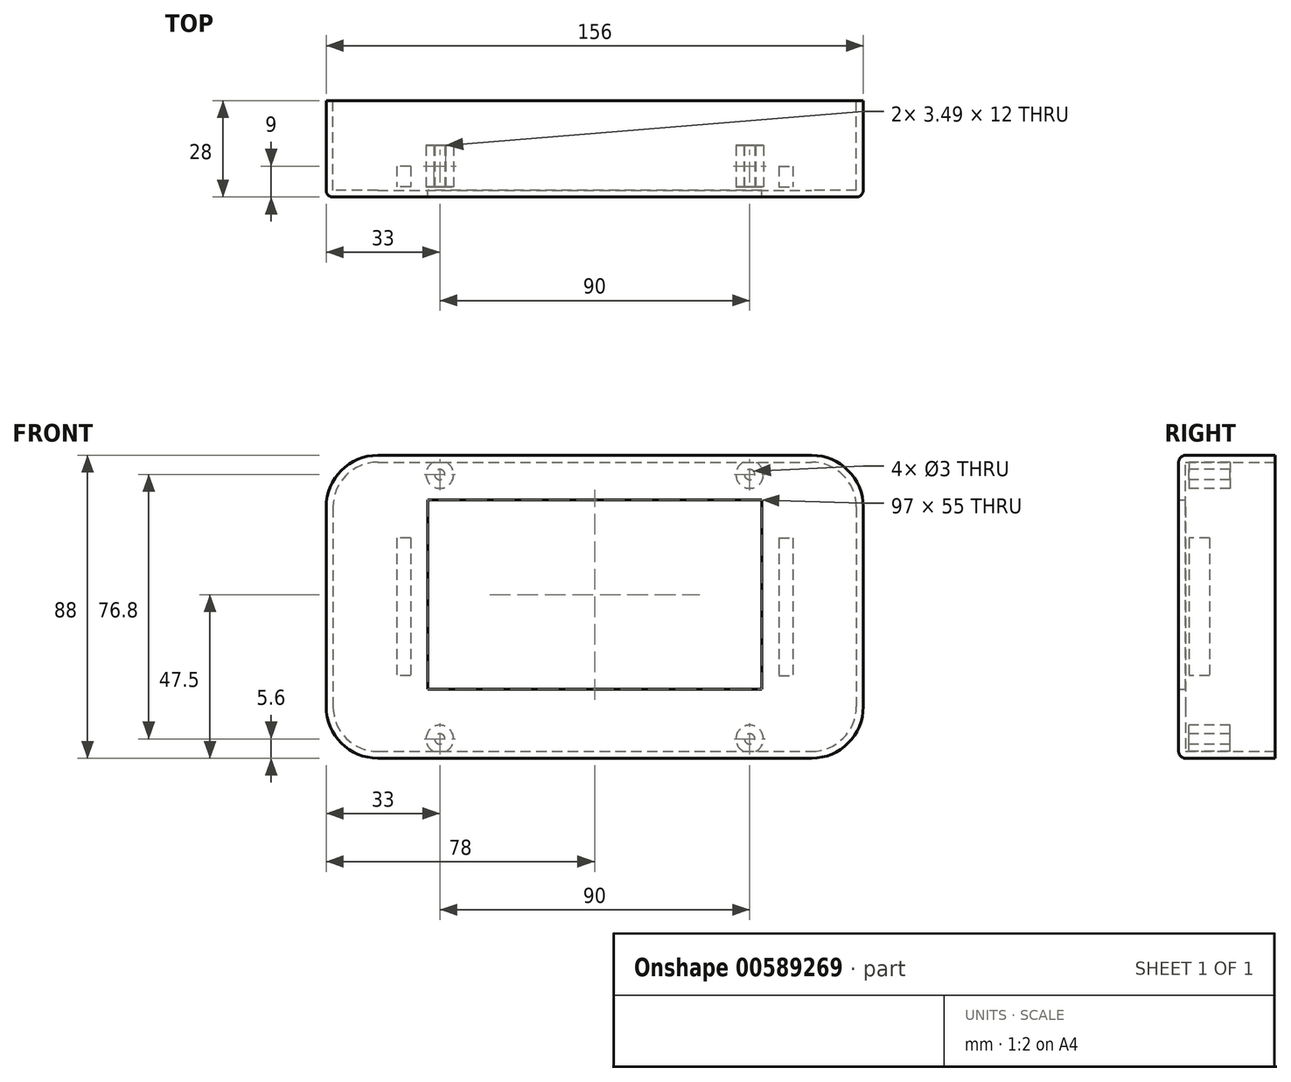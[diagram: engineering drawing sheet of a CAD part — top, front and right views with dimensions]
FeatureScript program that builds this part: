
annotation { "Feature Type Name" : "Feature", "Feature Type Description" : "" }
export const myFeature = defineFeature(function(context is Context, id is Id, definition is map)
    precondition{}
    {
        {
            var Q0;
            Q0=qCreatedBy(makeId("Front.planeOp"),FACE);
            var sketch = newSketch(context, id + "F0", { "sketchPlane" : qUnion([Q0])});
            skLineSegment(sketch, "E0.bottom", {"start": v(-63, 44) * mm, "end": v(63, 44) * mm});
            skLineSegment(sketch, "E0.top", {"start": v(-63, -44) * mm, "end": v(63, -44) * mm});
            skLineSegment(sketch, "E0.left", {"start": v(-78, 29) * mm, "end": v(-78, -29) * mm});
            skLineSegment(sketch, "E0.right", {"start": v(78, 29) * mm, "end": v(78, -29) * mm});
            skPoint(sketch, "E0.middle", {"position": v(0, 0) * mm});
            skPoint(sketch, "E1.visualSharp", {"position": v(-78, 44) * mm});
            skArc(sketch, "E1.filletArc", {"start": v(-63, 44) * mm, "mid": v(-73.6, 39.6) * mm, "end": v(-78, 29) * mm});
            skPoint(sketch, "E2.visualSharp", {"position": v(78, 44) * mm});
            skArc(sketch, "E2.filletArc", {"start": v(78, 29) * mm, "mid": v(73.6, 39.6) * mm, "end": v(63, 44) * mm});
            skPoint(sketch, "E3.visualSharp", {"position": v(78, -44) * mm});
            skArc(sketch, "E3.filletArc", {"start": v(63, -44) * mm, "mid": v(73.6, -39.6) * mm, "end": v(78, -29) * mm});
            skPoint(sketch, "E4.visualSharp", {"position": v(-78, -44) * mm});
            skArc(sketch, "E4.filletArc", {"start": v(-78, -29) * mm, "mid": v(-73.6, -39.6) * mm, "end": v(-63, -44) * mm});
            skSolve(sketch);
        }
        {
            var Q0;
            Q0=qSketchRegion(id+"F0",true);
            extrude(context, id + "F1", {"entities" : qUnion([Q0]), "depth" : 28 * mm, "offsetDistance" : 25 * mm});
        }
        {
            var Q0;
            Q0=makeQuery(id+"F1.opExtrude","CAP_FACE",FACE,{"disambiguationData":[OSD([sQuery(id+"F0.wireOp",EDGE,"E0.bottom"),sQuery(id+"F0.wireOp",EDGE,"E0.top"),sQuery(id+"F0.wireOp",EDGE,"E0.left"),sQuery(id+"F0.wireOp",EDGE,"E0.right"),sQuery(id+"F0.wireOp",EDGE,"E1.filletArc"),sQuery(id+"F0.wireOp",EDGE,"E2.filletArc"),sQuery(id+"F0.wireOp",EDGE,"E3.filletArc"),sQuery(id+"F0.wireOp",EDGE,"E4.filletArc")])],"isStart":true});
            shell(context, id + "F2", {"entities" : qUnion([Q0]), "thickness" : 2 * mm});
        }
        {
            var Q0;
            Q0=qCreatedBy(makeId("Front.planeOp"),FACE);
            cPlane(context, id + "F3", {"entities" : qUnion([Q0]), "cplaneType" : CPlaneType.OFFSET, "offset" : 25 * mm, "width" : 150 * mm, "height" : 150 * mm});
        }
        {
            var Q0;
            Q0=qCreatedBy(makeId("Front.planeOp"),FACE);
            var sketch = newSketch(context, id + "F4", { "sketchPlane" : qUnion([Q0])});
            skLineSegment(sketch, "E5.bottom", {"start": v(-48.5, 31) * mm, "end": v(48.5, 31) * mm});
            skLineSegment(sketch, "E5.top", {"start": v(-48.5, -24) * mm, "end": v(48.5, -24) * mm});
            skLineSegment(sketch, "E5.left", {"start": v(-48.5, 31) * mm, "end": v(-48.5, -24) * mm});
            skLineSegment(sketch, "E5.right", {"start": v(48.5, 31) * mm, "end": v(48.5, -24) * mm});
            skSolve(sketch);
        }
        {
            var Q0;
            Q0=makeQuery(id+"F4.imprint","IMPRINT",FACE,{"disambiguationData":[TD([[makeQuery(id+"F4.imprint","IMPRINT",EDGE,{"derivedFrom":sQuery(id+"F4.wireOp",EDGE,"E5.bottom")}),-1.0]])]});
            extrude(context, id + "F5", {"entities" : qUnion([Q0]), "operationType" : NewBodyOperationType.REMOVE, "depth" : 50 * mm});
        }
        {
            var Q0;
            Q0=qCreatedBy(id+"F3.planeOp",FACE);
            var sketch = newSketch(context, id + "F6", { "sketchPlane" : qUnion([Q0])});
            skLineSegment(sketch, "E6.bottom", {"start": v(53.5, 20) * mm, "end": v(57.5, 20) * mm});
            skLineSegment(sketch, "E6.top", {"start": v(53.5, -20) * mm, "end": v(57.5, -20) * mm});
            skLineSegment(sketch, "E6.left", {"start": v(53.5, 20) * mm, "end": v(53.5, -20) * mm});
            skLineSegment(sketch, "E6.right", {"start": v(57.5, 20) * mm, "end": v(57.5, -20) * mm});
            skPoint(sketch, "E6.middle", {"position": v(55.5, 0) * mm});
            skLineSegment(sketch, "E7", {"start": v(0, 34.27) * mm, "end": v(0, -34.37) * mm});
            skLineSegment(sketch, "E8.MirrorCS", {"start": v(-53.5, 20) * mm, "end": v(-53.5, -20) * mm});
            skLineSegment(sketch, "E9.MirrorCS", {"start": v(-53.5, 20) * mm, "end": v(-57.5, 20) * mm});
            skLineSegment(sketch, "E10.MirrorCS", {"start": v(-57.5, 20) * mm, "end": v(-57.5, -20) * mm});
            skLineSegment(sketch, "E11.MirrorCS", {"start": v(-53.5, -20) * mm, "end": v(-57.5, -20) * mm});
            skSolve(sketch);
        }
        {
            var Q0;
            Q0=qSketchRegion(id+"F6",true);
            extrude(context, id + "F7", {"entities" : qUnion([Q0]), "operationType" : NewBodyOperationType.ADD, "oppositeDirection" : true, "depth" : 6 * mm, "offsetDistance" : 25 * mm});
        }
        {
            var Q0;
            Q0=makeQuery(id+"F1.opExtrude","CAP_EDGE",EDGE,{"disambiguationData":[OSD([sQuery(id+"F0.wireOp",EDGE,"E0.bottom")])],"isStart":false});
            var Q1;
            Q1=makeQuery(id+"F1.opExtrude","CAP_EDGE",EDGE,{"disambiguationData":[OSD([sQuery(id+"F0.wireOp",EDGE,"E0.right")])],"isStart":false});
            fillet(context, id + "F8", {"entities" : qUnion([Q0, Q1]), "radius" : 2 * mm, "tangentPropagation" : true, "allowEdgeOverflow" : false});
        }
        {
            var Q0;
            Q0=qCreatedBy(makeId("Right.planeOp"),FACE);
            var sketch = newSketch(context, id + "F9", { "sketchPlane" : qUnion([Q0])});
            skCircle(sketch, "E12", {"center": v(-3, 0) * mm, "radius": 1.5 * mm});
            skSolve(sketch);
        }
        {
            var Q0;
            Q0=qCreatedBy(id+"F3.planeOp",FACE);
            var sketch = newSketch(context, id + "F10", { "sketchPlane" : qUnion([Q0])});
            skCircle(sketch, "E13", {"center": v(45, 38.4) * mm, "radius": 4 * mm});
            skCircle(sketch, "E14", {"center": v(45, 38.4) * mm, "radius": 1.5 * mm});
            skCircle(sketch, "E15.MirrorC", {"center": v(-45, 38.4) * mm, "radius": 4 * mm});
            skCircle(sketch, "E16.MirrorC", {"center": v(-45, 38.4) * mm, "radius": 1.5 * mm});
            skCircle(sketch, "E17.MirrorC", {"center": v(45, -38.4) * mm, "radius": 4 * mm});
            skCircle(sketch, "E18.MirrorC", {"center": v(45, -38.4) * mm, "radius": 1.5 * mm});
            skCircle(sketch, "E19.MirrorC", {"center": v(-45, -38.4) * mm, "radius": 4 * mm});
            skCircle(sketch, "E20.MirrorC", {"center": v(-45, -38.4) * mm, "radius": 1.5 * mm});
            skSolve(sketch);
        }
        {
            var Q0;
            Q0 = qSketchRegion(id + "F10", true);
            extrude(context, id + "F11", {"entities" : qUnion([Q0]), "operationType" : NewBodyOperationType.ADD, "oppositeDirection" : true, "depth" : 12 * mm, "offsetDistance" : 25 * mm});
        }
    });
